# Revit family: ID313
name_source: partatom
category: Apparecchi idraulici
units: mm (PartAtom-declared; Revit-internal decimal feet)

## family parameters
Basato su piano di lavoro = No
Condiviso = No
Mantieni orientamento annotazione = No
Numero OmniClass = 23.45.55.17
Punto di calcolo locali = No
Quota connettore circolare = Usa diametro
Sempre verticale = Sì
Taglio con vuoti quando caricato = No
Tipo di parte = Normale
Titolo OmniClass = Mixing Faucets

## types (12) — shared parameters
Cold water inlet = 10 mm  [stored 0.0328084 ft]
Commenti sul tipo = Wall mixer
Connessione CW = No
Connessione HW = No
Connessione di scarico = No
Connessione di ventilazione = No
Descrizione = Exposed parts for manual wall mixer with two ways diverter and shower kit
Hot water inlet = 10 mm  [stored 0.0328084 ft]
Produttore = IB Rubinetterie S.p.A.
URL = https://www.weareib.it
zero-valued in all types: Prospetto di default

## per-type parameters (varying)
| type | Finishes surface | Immagine tipo | Modello |
| Chrome | IB_Chrome | ID313CC.jpg | ID313CC |
| Brushed nickel | IB_Brushed nickel | ID313SS.jpg | ID313SS |
| Natural brass | IB_Brass | ID313ON.jpg | ID313ON |
| Matt black | IB_matt black | ID313NP.jpg | ID313NP |
| Black chrome | IB_Black chrome | ID313CF.jpg | ID313CF |
| Brushed black chrome | IB_Brushed black chrome | ID313CS.jpg | ID313CS |
| Pale gold | IB_Pale gold | ID313II.jpg | ID313II |
| Brushed pale gold | IB_brushed pale gold | ID313IS.jpg | ID313IS |
| Rose gold | IB_Rose gold | ID313RS.jpg | ID313RS |
| Brushed rose gold | IB_Brushed rose gold | ID313SR.jpg | ID313SR |
| Gold | IB_gold | ID313OO.jpg | ID313OO |
| Brushed gold | IB_brushed gold | ID313OS.jpg | ID313OS |

note: [stored X ft] marks values corroborated as IEEE doubles in the binary element streams (Revit-internal decimal feet)
